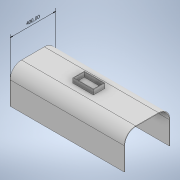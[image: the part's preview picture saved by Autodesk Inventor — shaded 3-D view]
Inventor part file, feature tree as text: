
AUTODESK INVENTOR PART (.ipt)
format: ipt  version: 2020 (Build 240168000, 168)  size: 131,584 bytes
history: native  units: mm
features: other x2, extrude x2, shell x2, sketch x2, fillet x1
ambient origin geometry x8: Origin, YZ Plane, XZ Plane, XY Plane, X Axis, Y Axis, Z Axis, Center Point
bodies: Solid1 (feature_tree)
feature tree (9):
  other  "Annotations"
  extrude  "Extrusion1"  Depth=400.0mm
  fillet  "Fillet1"  Radius=300.0mm
  shell  "Shell1"  Thickness=100.0mm
  extrude  "Extrusion2"  Depth=180.0mm
  shell  "Shell2"  Thickness=100.0mm
  sketch  "Sketch1"  dims[d0=1000.0mm d1=400.0mm d2=300.0mm d3=0.0mm d4=100.0mm]
  sketch  "Sketch2"  dims[d5=5.0mm d6=180.0mm d7=100.0mm d8=400.0mm d9=50.0mm d10=40.0mm d11=0.0mm d12=5.0mm d13=400.0mm]
  other  "Linear Dimension 1"
